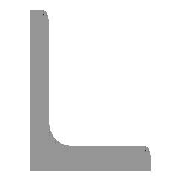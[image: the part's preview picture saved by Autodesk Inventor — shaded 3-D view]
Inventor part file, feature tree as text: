
AUTODESK INVENTOR PART (.ipt)
format: ipt  version: 2022 (Build 260153000, 153)  size: 135,680 bytes
history: native  units: mm (DEFAULTED — no unit token found)
features: other x4, sketch x3, plane x1
ambient origin geometry x8: Origin, YZ Plane, XZ Plane, XY Plane, X Axis, Y Axis, Z Axis, Center Point
bodies: Solid1 (feature_tree), Body (feature_tree)
feature tree (8):
  parser-record x1  (decoder bookkeeping rows leaked as tree rows — omitted from the tree; the rows remain in map.json)
  other  "Driven Length"
  other  "Start Plane"
  other  "End Plane"
  sketch  "Sketch"  dims[d5=50.0mm d6=30.0mm d7=4.0mm d8=3.0mm d9=4.0mm d10=3.0mm d11=1780.0mm d12=0.0mm d17=5.0mm d18=2.5mm d19=8.3mm d20=8.3mm d21=-0.0mm d22=1780.0mm d23=90.0deg d24=1780.0mm]
  sketch  "Sketch3"  dims[d3=50.0mm]
  plane  "Work Plane10"
  sketch  "Sketch4"  dims[d4=30.0mm]
